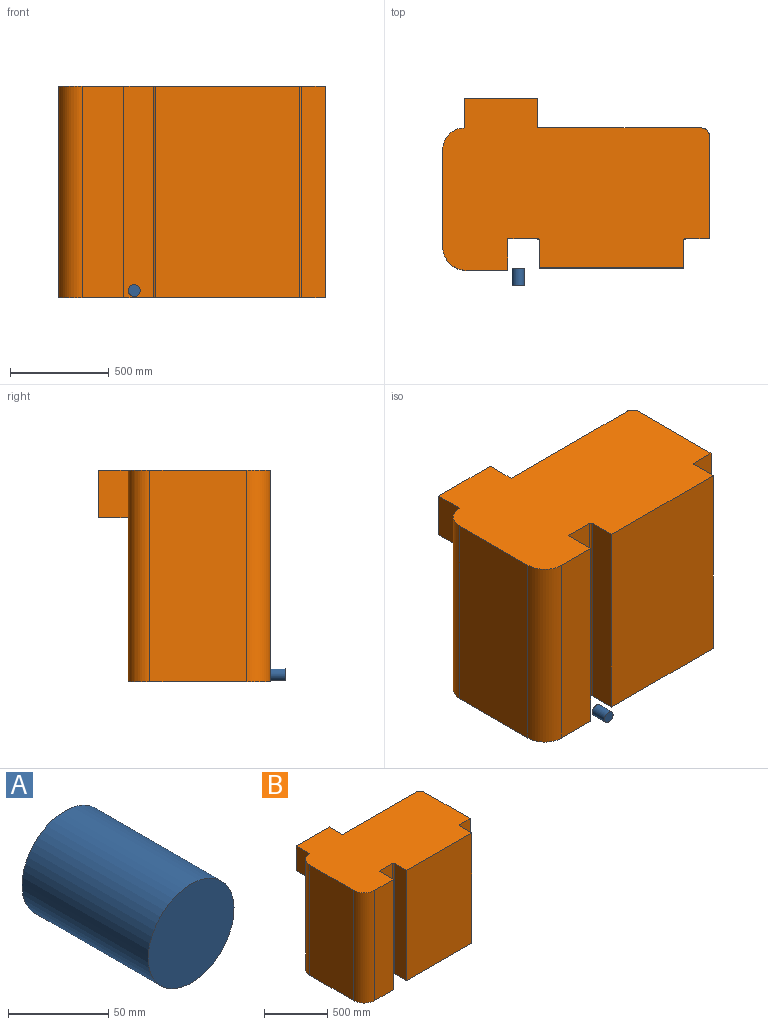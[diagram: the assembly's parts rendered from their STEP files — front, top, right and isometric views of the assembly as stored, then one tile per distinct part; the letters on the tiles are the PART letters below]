
ASSEMBLY  parts=2 mates=1
PART A: 3 faces, bbox 60.3x88.9x60.3 mm
  f0: cylinder r=30.16mm len=88.9mm, axis (0,1,0), area 16848mm2, adj f1,f2
  f1: plane 60.33x60.33mm, normal (0,-1,0), area 2858.1mm2, adj f0
  f2: plane 60.33x60.33mm, normal (0,1,0), area 2858.1mm2, adj f0
PART B: 21 faces, bbox 1350x870x1070 mm
  f0: plane 1200x1070mm, normal (0,1,0), area 1195200mm2, adj f6,f7,f13,f14,f17,f18
  f1: plane 1070x138.41mm, normal (-1,0,0), area 148098.7mm2, adj f2,f13,f14,f16
  f2: plane 1070x730mm, normal (0,-1,0), area 781100mm2, adj f1,f3,f13,f14
  f3: plane 1070x138.41mm, normal (1,0,0), area 148098.7mm2, adj f2,f13,f14,f15
  f4: plane 1070x121.11mm, normal (0,-1,0), area 129587.7mm2, adj f5,f13,f14,f15
  f5: plane 1070x520mm, normal (1,0,0), area 556400mm2, adj f4,f6,f13,f14
  f6: cylinder r=40mm len=1070mm, axis (0,0,-1), area 67230.1mm2, adj f0,f5,f13,f14
  f7: cylinder r=110mm len=1070mm, axis (0,0,-1), area 184882.7mm2, adj f0,f8,f13,f14,f19
  f8: plane 1070x490mm, normal (-1,0,0), area 524300mm2, adj f7,f9,f13,f14
  f9: cylinder r=120mm len=1070mm, axis (0,0,-1), area 201690.2mm2, adj f8,f10,f13,f14
  f10: plane 1070x210mm, normal (0,-1,0), area 224700mm2, adj f9,f11,f13,f14
  f11: plane 1070x160mm, normal (1,0,0), area 171200mm2, adj f10,f12,f13,f14
  f12: plane 1070x151.11mm, normal (0,-1,0), area 161687.7mm2, adj f11,f13,f14,f16
  f13: plane 1350x870mm, normal (0,0,1), area 965832.6mm2, adj f0,f1,f2,f3,f4,f5,f6,f7
  f14: plane 1350x720mm, normal (0,0,-1), area 910332.6mm2, adj f0,f1,f2,f3,f4,f5,f6,f7
  f15: cylinder r=8.89mm len=1070mm, axis (0,0,-1), area 14941.9mm2, adj f3,f4,f13,f14
  f16: cylinder r=8.89mm len=1070mm, axis (0,0,1), area 14941.9mm2, adj f1,f12,f13,f14
  f17: plane 240x150mm, normal (1,0,0), area 36000mm2, adj f0,f13,f18,f20
  f18: plane 370x150mm, normal (0,0,-1), area 55500mm2, adj f0,f17,f19,f20
  f19: plane 240x150mm, normal (-1,0,0), area 36000mm2, adj f7,f13,f18,f20
  f20: plane 370x240mm, normal (0,1,0), area 88800mm2, adj f13,f17,f18,f19
PLACE A t=(23.27,26.24,22.93)mm
PLACE B t=(-18.91,45.69,-13.7)mm
MATE parallel A.f0 <-> B.f2  axis (0,1,0) through (23.27,26.24,22.93)mm
